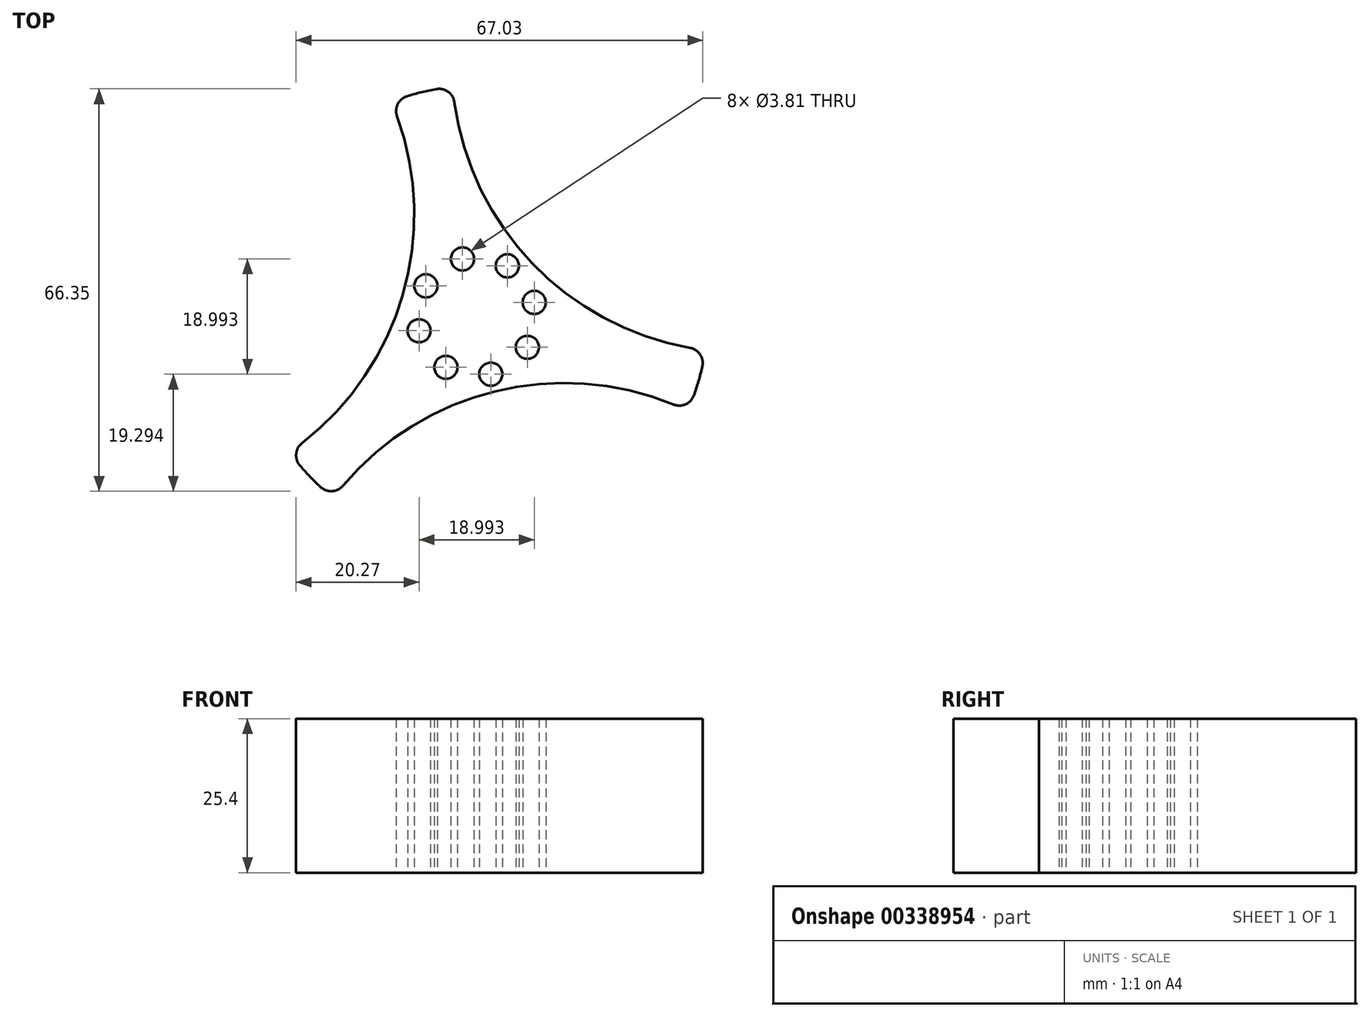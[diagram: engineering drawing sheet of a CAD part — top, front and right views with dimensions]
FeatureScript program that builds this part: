
annotation { "Feature Type Name" : "Feature", "Feature Type Description" : "" }
export const myFeature = defineFeature(function(context is Context, id is Id, definition is map)
    precondition{}
    {
        {
            var Q0;
            Q0=qCreatedBy(makeId("Top.planeOp"),FACE);
            var sketch = newSketch(context, id + "F0", { "sketchPlane" : qUnion([Q0])});
            skCircle(sketch, "E0", {"center": v(-114.93, 57.44) * mm, "radius": 12.7 * mm});
            skArc(sketch, "E1", {"start": v(-144.1, 32.93) * mm, "mid": v(-142.43, 31.07) * mm, "end": v(-140.64, 29.32) * mm});
            skArc(sketch, "E2", {"start": v(-121.57, 94.96) * mm, "mid": v(-124.02, 94.44) * mm, "end": v(-126.43, 93.76) * mm});
            skArc(sketch, "E3", {"start": v(-79.12, 44.43) * mm, "mid": v(-78.35, 46.81) * mm, "end": v(-77.73, 49.24) * mm});
            skArc(sketch, "E4", {"start": v(-143.72, 36.57) * mm, "mid": v(-127.13, 60.98) * mm, "end": v(-128.06, 90.48) * mm});
            skArc(sketch, "E5", {"start": v(-118.61, 92.8) * mm, "mid": v(-105.77, 66.23) * mm, "end": v(-79.76, 52.29) * mm});
            skArc(sketch, "E6", {"start": v(-82.47, 42.95) * mm, "mid": v(-111.9, 45.1) * mm, "end": v(-136.99, 29.55) * mm});
            skPoint(sketch, "E7.visualSharp", {"position": v(-128.98, 92.86) * mm});
            skArc(sketch, "E7.filletArc", {"start": v(-126.43, 93.76) * mm, "mid": v(-127.94, 92.47) * mm, "end": v(-128.06, 90.48) * mm});
            skPoint(sketch, "E8.visualSharp", {"position": v(-118.9, 95.33) * mm});
            skArc(sketch, "E8.filletArc", {"start": v(-118.61, 92.8) * mm, "mid": v(-119.63, 94.5) * mm, "end": v(-121.57, 94.96) * mm});
            skPoint(sketch, "E9.visualSharp", {"position": v(-77.24, 51.9) * mm});
            skArc(sketch, "E9.filletArc", {"start": v(-77.73, 49.24) * mm, "mid": v(-78.1, 51.2) * mm, "end": v(-79.76, 52.29) * mm});
            skPoint(sketch, "E10.visualSharp", {"position": v(-80.14, 41.92) * mm});
            skArc(sketch, "E10.filletArc", {"start": v(-82.47, 42.95) * mm, "mid": v(-80.48, 42.98) * mm, "end": v(-79.12, 44.43) * mm});
            skPoint(sketch, "E11.visualSharp", {"position": v(-138.58, 27.57) * mm});
            skArc(sketch, "E11.filletArc", {"start": v(-140.64, 29.32) * mm, "mid": v(-138.76, 28.66) * mm, "end": v(-136.99, 29.55) * mm});
            skPoint(sketch, "E12.visualSharp", {"position": v(-145.77, 35.07) * mm});
            skArc(sketch, "E12.filletArc", {"start": v(-143.72, 36.57) * mm, "mid": v(-144.69, 34.84) * mm, "end": v(-144.1, 32.93) * mm});
            skCircle(sketch, "E13", {"center": v(-114.93, 57.44) * mm, "radius": 9.78 * mm});
            skLineSegment(sketch, "E14", {"start": v(-124.02, 94.44) * mm, "end": v(-114.93, 57.44) * mm});
            skCircle(sketch, "E15", {"center": v(-117.27, 66.94) * mm, "radius": 1.9 * mm});
            skCircle(sketch, "E16.1.0", {"center": v(-123.3, 62.5) * mm, "radius": 1.9 * mm});
            skCircle(sketch, "E16.2.0", {"center": v(-124.43, 55.1) * mm, "radius": 1.9 * mm});
            skCircle(sketch, "E16.3.0", {"center": v(-120, 49.08) * mm, "radius": 1.9 * mm});
            skCircle(sketch, "E16.4.0", {"center": v(-112.6, 47.94) * mm, "radius": 1.9 * mm});
            skCircle(sketch, "E16.5.0", {"center": v(-106.57, 52.38) * mm, "radius": 1.9 * mm});
            skCircle(sketch, "E16.6.0", {"center": v(-105.44, 59.77) * mm, "radius": 1.9 * mm});
            skCircle(sketch, "E16.7.0", {"center": v(-109.87, 65.8) * mm, "radius": 1.9 * mm});
            skSolve(sketch);
        }
        {
            var Q0;
            Q0=makeQuery(id+"F0.imprint","IMPRINT",FACE,{"disambiguationData":[TD([[makeQuery(id+"F0.imprint","IMPRINT",EDGE,{"derivedFrom":sQuery(id+"F0.wireOp",EDGE,"E3")}),1.0]])]});
            var Q1;
            Q1=makeQuery(id+"F0.imprint","IMPRINT",FACE,{"disambiguationData":[TD([[makeQuery(id+"F0.imprint","IMPRINT",EDGE,{"derivedFrom":sQuery(id+"F0.wireOp",EDGE,"E1")}),1.0]])]});
            var Q2;
            {var subQ0=sQuery(id+"F0.wireOp",EDGE,"E8.filletArc");Q2=makeQuery(id+"F0.imprint","IMPRINT",FACE,{"disambiguationData":[TD([[makeQuery(id+"F0.imprint","IMPRINT",EDGE,{"derivedFrom":subQ0}),1.0]])]});}
            var Q3;
            {var subQ0=sQuery(id+"F0.wireOp",EDGE,"E7.filletArc");Q3=makeQuery(id+"F0.imprint","IMPRINT",FACE,{"disambiguationData":[TD([[makeQuery(id+"F0.imprint","IMPRINT",EDGE,{"derivedFrom":subQ0}),1.0]])]});}
            var Q4;
            {var subQ2=sQuery(id+"F0.wireOp",EDGE,"E13");var subQ4=sQuery(id+"F0.wireOp",EDGE,"E16.6.0");var subQ17=makeQuery(id+"F0.imprint","INTERSECT",VERTEX,{"disambiguationData":[OD(0.0)],"derivedFrom":[subQ2,subQ4]});Q4=makeQuery(id+"F0.imprint","IMPRINT",FACE,{"disambiguationData":[TD([[makeQuery(id+"F0.imprint","IMPRINT",EDGE,{"disambiguationData":[TD([[subQ17,-1.0]])],"derivedFrom":subQ2}),1.0]])]});}
            var Q5;
            {var subQ11=sQuery(id+"F0.wireOp",EDGE,"E0");var subQ21=sQuery(id+"F0.wireOp",EDGE,"E14");var subQ22=makeQuery(id+"F0.imprint","INTERSECT",VERTEX,{"derivedFrom":[subQ11,subQ21]});Q5=makeQuery(id+"F0.imprint","IMPRINT",FACE,{"disambiguationData":[TD([[makeQuery(id+"F0.imprint","IMPRINT",EDGE,{"disambiguationData":[TD([[subQ22,1.0]])],"derivedFrom":subQ11}),1.0]])]});}
            extrude(context, id + "F1", {"entities" : qUnion([Q0, Q1, Q2, Q3, Q4, Q5]), "depth" : 12.7 * mm, "hasSecondDirection" : true, "secondDirectionOppositeDirection" : true, "secondDirectionDepth" : 12.7 * mm});
        }
    });
